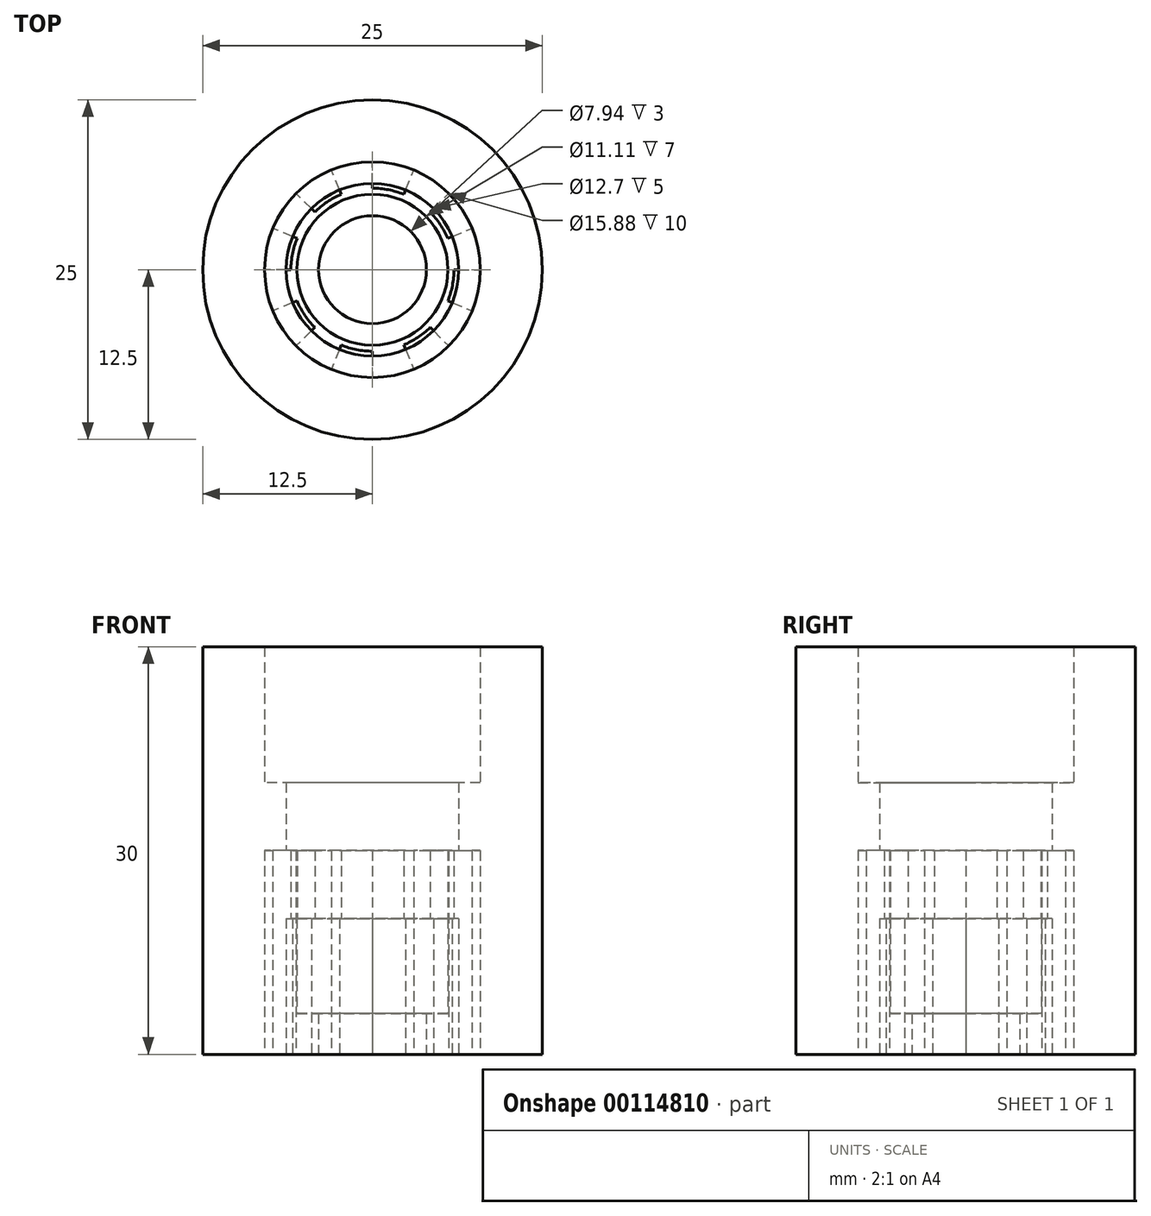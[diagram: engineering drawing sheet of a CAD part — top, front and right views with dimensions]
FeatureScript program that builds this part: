
annotation { "Feature Type Name" : "Feature", "Feature Type Description" : "" }
export const myFeature = defineFeature(function(context is Context, id is Id, definition is map)
    precondition{}
    {
        {
            var Q0;
            Q0=qCreatedBy(makeId("Top.planeOp"),FACE);
            var sketch = newSketch(context, id + "F0", { "sketchPlane" : qUnion([Q0])});
            skCircle(sketch, "E0", {"center": v(0, 0) * mm, "radius": 12.5 * mm});
            skCircle(sketch, "E1", {"center": v(0, 0) * mm, "radius": 7.94 * mm});
            skCircle(sketch, "E2", {"center": v(0, 0) * mm, "radius": 5.56 * mm});
            skCircle(sketch, "E3", {"center": v(0, 0) * mm, "radius": 3.97 * mm});
            skCircle(sketch, "E4", {"center": v(0, 0) * mm, "radius": 6.35 * mm});
            skCircle(sketch, "E5", {"center": v(0, 0) * mm, "radius": 6 * mm});
            skCircle(sketch, "E6", {"center": v(0, 0) * mm, "radius": 8.5 * mm});
            skLineSegment(sketch, "E7", {"start": v(0, 5.56) * mm, "end": v(0, 8.5) * mm});
            skLineSegment(sketch, "E8.1.0", {"start": v(-2.13, 5.13) * mm, "end": v(-3.25, 7.85) * mm});
            skLineSegment(sketch, "E8.2.0", {"start": v(-3.93, 3.93) * mm, "end": v(-6.01, 6.01) * mm});
            skLineSegment(sketch, "E9.1.3.0", {"start": v(-5.13, 2.13) * mm, "end": v(-7.85, 3.25) * mm});
            skLineSegment(sketch, "E9.1.4.0", {"start": v(-5.56, 0) * mm, "end": v(-8.5, 0) * mm});
            skLineSegment(sketch, "E9.1.5.0", {"start": v(-5.13, -2.13) * mm, "end": v(-7.85, -3.25) * mm});
            skLineSegment(sketch, "E9.1.6.0", {"start": v(-3.93, -3.93) * mm, "end": v(-6.01, -6.01) * mm});
            skLineSegment(sketch, "E9.1.7.0", {"start": v(-2.13, -5.13) * mm, "end": v(-3.25, -7.85) * mm});
            skLineSegment(sketch, "E9.1.8.0", {"start": v(0, -5.56) * mm, "end": v(0, -8.5) * mm});
            skLineSegment(sketch, "E9.1.9.0", {"start": v(2.13, -5.13) * mm, "end": v(3.25, -7.85) * mm});
            skLineSegment(sketch, "E9.1.10.0", {"start": v(3.93, -3.93) * mm, "end": v(6.01, -6.01) * mm});
            skLineSegment(sketch, "E9.1.11.0", {"start": v(5.13, -2.13) * mm, "end": v(7.85, -3.25) * mm});
            skLineSegment(sketch, "E10.1.12.0", {"start": v(5.56, 0) * mm, "end": v(8.5, 0) * mm});
            skLineSegment(sketch, "E10.1.13.0", {"start": v(5.13, 2.13) * mm, "end": v(7.85, 3.25) * mm});
            skLineSegment(sketch, "E10.1.14.0", {"start": v(3.93, 3.93) * mm, "end": v(6.01, 6.01) * mm});
            skLineSegment(sketch, "E10.1.15.0", {"start": v(2.13, 5.13) * mm, "end": v(3.25, 7.85) * mm});
            skSolve(sketch);
        }
        {
            var Q0;
            Q0=makeQuery(id+"F0.imprint","IMPRINT",FACE,{"disambiguationData":[TD([[makeQuery(id+"F0.imprint","IMPRINT",EDGE,{"derivedFrom":sQuery(id+"F0.wireOp",EDGE,"E3")}),-1.0]])]});
            extrude(context, id + "F1", {"entities" : qUnion([Q0]), "depth" : 3 * mm});
        }
        {
            var Q0;
            {var subQ0=sQuery(id+"F0.wireOp",EDGE,"E10.1.13.0");var subQ1=sQuery(id+"F0.wireOp",EDGE,"E2");var subQ2=makeQuery(id+"F0.imprint","INTERSECT",VERTEX,{"derivedFrom":[subQ1,subQ0]});Q0=makeQuery(id+"F0.imprint","IMPRINT",FACE,{"disambiguationData":[TD([[makeQuery(id+"F0.imprint","IMPRINT",EDGE,{"disambiguationData":[TD([[subQ2,-1.0]])],"derivedFrom":subQ1}),-1.0]])]});}
            var Q1;
            {var subQ0=sQuery(id+"F0.wireOp",EDGE,"E10.1.12.0");var subQ1=sQuery(id+"F0.wireOp",EDGE,"E2");var subQ2=makeQuery(id+"F0.imprint","INTERSECT",VERTEX,{"derivedFrom":[subQ1,subQ0]});Q1=makeQuery(id+"F0.imprint","IMPRINT",FACE,{"disambiguationData":[TD([[makeQuery(id+"F0.imprint","IMPRINT",EDGE,{"disambiguationData":[TD([[subQ2,-1.0]])],"derivedFrom":subQ1}),-1.0]])]});}
            var Q2;
            {var subQ0=sQuery(id+"F0.wireOp",EDGE,"E9.1.11.0");var subQ1=sQuery(id+"F0.wireOp",EDGE,"E2");var subQ2=makeQuery(id+"F0.imprint","INTERSECT",VERTEX,{"derivedFrom":[subQ1,subQ0]});Q2=makeQuery(id+"F0.imprint","IMPRINT",FACE,{"disambiguationData":[TD([[makeQuery(id+"F0.imprint","IMPRINT",EDGE,{"disambiguationData":[TD([[subQ2,-1.0]])],"derivedFrom":subQ1}),-1.0]])]});}
            var Q3;
            {var subQ0=sQuery(id+"F0.wireOp",EDGE,"E9.1.10.0");var subQ1=sQuery(id+"F0.wireOp",EDGE,"E2");var subQ2=makeQuery(id+"F0.imprint","INTERSECT",VERTEX,{"derivedFrom":[subQ1,subQ0]});Q3=makeQuery(id+"F0.imprint","IMPRINT",FACE,{"disambiguationData":[TD([[makeQuery(id+"F0.imprint","IMPRINT",EDGE,{"disambiguationData":[TD([[subQ2,-1.0]])],"derivedFrom":subQ1}),-1.0]])]});}
            var Q4;
            {var subQ0=sQuery(id+"F0.wireOp",EDGE,"E9.1.9.0");var subQ1=sQuery(id+"F0.wireOp",EDGE,"E2");var subQ2=makeQuery(id+"F0.imprint","INTERSECT",VERTEX,{"derivedFrom":[subQ1,subQ0]});Q4=makeQuery(id+"F0.imprint","IMPRINT",FACE,{"disambiguationData":[TD([[makeQuery(id+"F0.imprint","IMPRINT",EDGE,{"disambiguationData":[TD([[subQ2,-1.0]])],"derivedFrom":subQ1}),-1.0]])]});}
            var Q5;
            {var subQ0=sQuery(id+"F0.wireOp",EDGE,"E9.1.8.0");var subQ1=sQuery(id+"F0.wireOp",EDGE,"E2");var subQ2=makeQuery(id+"F0.imprint","INTERSECT",VERTEX,{"derivedFrom":[subQ1,subQ0]});Q5=makeQuery(id+"F0.imprint","IMPRINT",FACE,{"disambiguationData":[TD([[makeQuery(id+"F0.imprint","IMPRINT",EDGE,{"disambiguationData":[TD([[subQ2,-1.0]])],"derivedFrom":subQ1}),-1.0]])]});}
            var Q6;
            {var subQ0=sQuery(id+"F0.wireOp",EDGE,"E9.1.7.0");var subQ1=sQuery(id+"F0.wireOp",EDGE,"E2");var subQ2=makeQuery(id+"F0.imprint","INTERSECT",VERTEX,{"derivedFrom":[subQ1,subQ0]});Q6=makeQuery(id+"F0.imprint","IMPRINT",FACE,{"disambiguationData":[TD([[makeQuery(id+"F0.imprint","IMPRINT",EDGE,{"disambiguationData":[TD([[subQ2,-1.0]])],"derivedFrom":subQ1}),-1.0]])]});}
            var Q7;
            {var subQ0=sQuery(id+"F0.wireOp",EDGE,"E9.1.6.0");var subQ1=sQuery(id+"F0.wireOp",EDGE,"E2");var subQ2=makeQuery(id+"F0.imprint","INTERSECT",VERTEX,{"derivedFrom":[subQ1,subQ0]});Q7=makeQuery(id+"F0.imprint","IMPRINT",FACE,{"disambiguationData":[TD([[makeQuery(id+"F0.imprint","IMPRINT",EDGE,{"disambiguationData":[TD([[subQ2,-1.0]])],"derivedFrom":subQ1}),-1.0]])]});}
            var Q8;
            {var subQ0=sQuery(id+"F0.wireOp",EDGE,"E9.1.5.0");var subQ1=sQuery(id+"F0.wireOp",EDGE,"E2");var subQ2=makeQuery(id+"F0.imprint","INTERSECT",VERTEX,{"derivedFrom":[subQ1,subQ0]});Q8=makeQuery(id+"F0.imprint","IMPRINT",FACE,{"disambiguationData":[TD([[makeQuery(id+"F0.imprint","IMPRINT",EDGE,{"disambiguationData":[TD([[subQ2,-1.0]])],"derivedFrom":subQ1}),-1.0]])]});}
            var Q9;
            {var subQ0=sQuery(id+"F0.wireOp",EDGE,"E9.1.4.0");var subQ1=sQuery(id+"F0.wireOp",EDGE,"E2");var subQ2=makeQuery(id+"F0.imprint","INTERSECT",VERTEX,{"derivedFrom":[subQ1,subQ0]});Q9=makeQuery(id+"F0.imprint","IMPRINT",FACE,{"disambiguationData":[TD([[makeQuery(id+"F0.imprint","IMPRINT",EDGE,{"disambiguationData":[TD([[subQ2,-1.0]])],"derivedFrom":subQ1}),-1.0]])]});}
            var Q10;
            {var subQ0=sQuery(id+"F0.wireOp",EDGE,"E10.1.14.0");var subQ1=sQuery(id+"F0.wireOp",EDGE,"E2");var subQ2=makeQuery(id+"F0.imprint","INTERSECT",VERTEX,{"derivedFrom":[subQ1,subQ0]});Q10=makeQuery(id+"F0.imprint","IMPRINT",FACE,{"disambiguationData":[TD([[makeQuery(id+"F0.imprint","IMPRINT",EDGE,{"disambiguationData":[TD([[subQ2,-1.0]])],"derivedFrom":subQ1}),-1.0]])]});}
            var Q11;
            {var subQ0=sQuery(id+"F0.wireOp",EDGE,"E7");var subQ1=sQuery(id+"F0.wireOp",EDGE,"E2");var subQ2=makeQuery(id+"F0.imprint","INTERSECT",VERTEX,{"derivedFrom":[subQ1,subQ0]});Q11=makeQuery(id+"F0.imprint","IMPRINT",FACE,{"disambiguationData":[TD([[makeQuery(id+"F0.imprint","IMPRINT",EDGE,{"disambiguationData":[TD([[subQ2,1.0]])],"derivedFrom":subQ1}),-1.0]])]});}
            var Q12;
            {var subQ0=sQuery(id+"F0.wireOp",EDGE,"E7");var subQ1=sQuery(id+"F0.wireOp",EDGE,"E2");var subQ2=makeQuery(id+"F0.imprint","INTERSECT",VERTEX,{"derivedFrom":[subQ1,subQ0]});Q12=makeQuery(id+"F0.imprint","IMPRINT",FACE,{"disambiguationData":[TD([[makeQuery(id+"F0.imprint","IMPRINT",EDGE,{"disambiguationData":[TD([[subQ2,-1.0]])],"derivedFrom":subQ1}),-1.0]])]});}
            var Q13;
            {var subQ0=sQuery(id+"F0.wireOp",EDGE,"E8.1.0");var subQ1=sQuery(id+"F0.wireOp",EDGE,"E2");var subQ2=makeQuery(id+"F0.imprint","INTERSECT",VERTEX,{"derivedFrom":[subQ1,subQ0]});Q13=makeQuery(id+"F0.imprint","IMPRINT",FACE,{"disambiguationData":[TD([[makeQuery(id+"F0.imprint","IMPRINT",EDGE,{"disambiguationData":[TD([[subQ2,-1.0]])],"derivedFrom":subQ1}),-1.0]])]});}
            var Q14;
            {var subQ0=sQuery(id+"F0.wireOp",EDGE,"E8.2.0");var subQ1=sQuery(id+"F0.wireOp",EDGE,"E2");var subQ2=makeQuery(id+"F0.imprint","INTERSECT",VERTEX,{"derivedFrom":[subQ1,subQ0]});Q14=makeQuery(id+"F0.imprint","IMPRINT",FACE,{"disambiguationData":[TD([[makeQuery(id+"F0.imprint","IMPRINT",EDGE,{"disambiguationData":[TD([[subQ2,-1.0]])],"derivedFrom":subQ1}),-1.0]])]});}
            var Q15;
            {var subQ0=sQuery(id+"F0.wireOp",EDGE,"E9.1.3.0");var subQ1=sQuery(id+"F0.wireOp",EDGE,"E2");var subQ2=makeQuery(id+"F0.imprint","INTERSECT",VERTEX,{"derivedFrom":[subQ1,subQ0]});Q15=makeQuery(id+"F0.imprint","IMPRINT",FACE,{"disambiguationData":[TD([[makeQuery(id+"F0.imprint","IMPRINT",EDGE,{"disambiguationData":[TD([[subQ2,-1.0]])],"derivedFrom":subQ1}),-1.0]])]});}
            var Q16;
            {var subQ0=sQuery(id+"F0.wireOp",EDGE,"E7");var subQ1=sQuery(id+"F0.wireOp",EDGE,"E4");var subQ2=makeQuery(id+"F0.imprint","INTERSECT",VERTEX,{"derivedFrom":[subQ1,subQ0]});Q16=makeQuery(id+"F0.imprint","IMPRINT",FACE,{"disambiguationData":[TD([[makeQuery(id+"F0.imprint","IMPRINT",EDGE,{"disambiguationData":[TD([[subQ2,-1.0]])],"derivedFrom":subQ1}),1.0]])]});}
            var Q17;
            {var subQ0=sQuery(id+"F0.wireOp",EDGE,"E8.1.0");var subQ1=sQuery(id+"F0.wireOp",EDGE,"E4");var subQ2=makeQuery(id+"F0.imprint","INTERSECT",VERTEX,{"derivedFrom":[subQ1,subQ0]});Q17=makeQuery(id+"F0.imprint","IMPRINT",FACE,{"disambiguationData":[TD([[makeQuery(id+"F0.imprint","IMPRINT",EDGE,{"disambiguationData":[TD([[subQ2,-1.0]])],"derivedFrom":subQ1}),1.0]])]});}
            var Q18;
            {var subQ0=sQuery(id+"F0.wireOp",EDGE,"E8.2.0");var subQ1=sQuery(id+"F0.wireOp",EDGE,"E4");var subQ2=makeQuery(id+"F0.imprint","INTERSECT",VERTEX,{"derivedFrom":[subQ1,subQ0]});Q18=makeQuery(id+"F0.imprint","IMPRINT",FACE,{"disambiguationData":[TD([[makeQuery(id+"F0.imprint","IMPRINT",EDGE,{"disambiguationData":[TD([[subQ2,-1.0]])],"derivedFrom":subQ1}),1.0]])]});}
            var Q19;
            {var subQ0=sQuery(id+"F0.wireOp",EDGE,"E10.1.15.0");var subQ1=sQuery(id+"F0.wireOp",EDGE,"E4");var subQ2=makeQuery(id+"F0.imprint","INTERSECT",VERTEX,{"derivedFrom":[subQ1,subQ0]});Q19=makeQuery(id+"F0.imprint","IMPRINT",FACE,{"disambiguationData":[TD([[makeQuery(id+"F0.imprint","IMPRINT",EDGE,{"disambiguationData":[TD([[subQ2,-1.0]])],"derivedFrom":subQ1}),1.0]])]});}
            var Q20;
            {var subQ0=sQuery(id+"F0.wireOp",EDGE,"E10.1.14.0");var subQ1=sQuery(id+"F0.wireOp",EDGE,"E4");var subQ2=makeQuery(id+"F0.imprint","INTERSECT",VERTEX,{"derivedFrom":[subQ1,subQ0]});Q20=makeQuery(id+"F0.imprint","IMPRINT",FACE,{"disambiguationData":[TD([[makeQuery(id+"F0.imprint","IMPRINT",EDGE,{"disambiguationData":[TD([[subQ2,-1.0]])],"derivedFrom":subQ1}),1.0]])]});}
            var Q21;
            {var subQ0=sQuery(id+"F0.wireOp",EDGE,"E10.1.13.0");var subQ1=sQuery(id+"F0.wireOp",EDGE,"E4");var subQ2=makeQuery(id+"F0.imprint","INTERSECT",VERTEX,{"derivedFrom":[subQ1,subQ0]});Q21=makeQuery(id+"F0.imprint","IMPRINT",FACE,{"disambiguationData":[TD([[makeQuery(id+"F0.imprint","IMPRINT",EDGE,{"disambiguationData":[TD([[subQ2,-1.0]])],"derivedFrom":subQ1}),1.0]])]});}
            var Q22;
            {var subQ0=sQuery(id+"F0.wireOp",EDGE,"E10.1.13.0");var subQ1=sQuery(id+"F0.wireOp",EDGE,"E4");var subQ2=makeQuery(id+"F0.imprint","INTERSECT",VERTEX,{"derivedFrom":[subQ1,subQ0]});Q22=makeQuery(id+"F0.imprint","IMPRINT",FACE,{"disambiguationData":[TD([[makeQuery(id+"F0.imprint","IMPRINT",EDGE,{"disambiguationData":[TD([[subQ2,1.0]])],"derivedFrom":subQ1}),1.0]])]});}
            var Q23;
            {var subQ0=sQuery(id+"F0.wireOp",EDGE,"E10.1.12.0");var subQ1=sQuery(id+"F0.wireOp",EDGE,"E4");var subQ2=makeQuery(id+"F0.imprint","INTERSECT",VERTEX,{"derivedFrom":[subQ1,subQ0]});Q23=makeQuery(id+"F0.imprint","IMPRINT",FACE,{"disambiguationData":[TD([[makeQuery(id+"F0.imprint","IMPRINT",EDGE,{"disambiguationData":[TD([[subQ2,1.0]])],"derivedFrom":subQ1}),1.0]])]});}
            var Q24;
            {var subQ0=sQuery(id+"F0.wireOp",EDGE,"E9.1.10.0");var subQ1=sQuery(id+"F0.wireOp",EDGE,"E4");var subQ2=makeQuery(id+"F0.imprint","INTERSECT",VERTEX,{"derivedFrom":[subQ1,subQ0]});Q24=makeQuery(id+"F0.imprint","IMPRINT",FACE,{"disambiguationData":[TD([[makeQuery(id+"F0.imprint","IMPRINT",EDGE,{"disambiguationData":[TD([[subQ2,-1.0]])],"derivedFrom":subQ1}),1.0]])]});}
            var Q25;
            {var subQ0=sQuery(id+"F0.wireOp",EDGE,"E9.1.9.0");var subQ1=sQuery(id+"F0.wireOp",EDGE,"E4");var subQ2=makeQuery(id+"F0.imprint","INTERSECT",VERTEX,{"derivedFrom":[subQ1,subQ0]});Q25=makeQuery(id+"F0.imprint","IMPRINT",FACE,{"disambiguationData":[TD([[makeQuery(id+"F0.imprint","IMPRINT",EDGE,{"disambiguationData":[TD([[subQ2,-1.0]])],"derivedFrom":subQ1}),1.0]])]});}
            var Q26;
            {var subQ0=sQuery(id+"F0.wireOp",EDGE,"E9.1.8.0");var subQ1=sQuery(id+"F0.wireOp",EDGE,"E4");var subQ2=makeQuery(id+"F0.imprint","INTERSECT",VERTEX,{"derivedFrom":[subQ1,subQ0]});Q26=makeQuery(id+"F0.imprint","IMPRINT",FACE,{"disambiguationData":[TD([[makeQuery(id+"F0.imprint","IMPRINT",EDGE,{"disambiguationData":[TD([[subQ2,-1.0]])],"derivedFrom":subQ1}),1.0]])]});}
            var Q27;
            {var subQ0=sQuery(id+"F0.wireOp",EDGE,"E9.1.7.0");var subQ1=sQuery(id+"F0.wireOp",EDGE,"E4");var subQ2=makeQuery(id+"F0.imprint","INTERSECT",VERTEX,{"derivedFrom":[subQ1,subQ0]});Q27=makeQuery(id+"F0.imprint","IMPRINT",FACE,{"disambiguationData":[TD([[makeQuery(id+"F0.imprint","IMPRINT",EDGE,{"disambiguationData":[TD([[subQ2,-1.0]])],"derivedFrom":subQ1}),1.0]])]});}
            var Q28;
            {var subQ0=sQuery(id+"F0.wireOp",EDGE,"E9.1.6.0");var subQ1=sQuery(id+"F0.wireOp",EDGE,"E4");var subQ2=makeQuery(id+"F0.imprint","INTERSECT",VERTEX,{"derivedFrom":[subQ1,subQ0]});Q28=makeQuery(id+"F0.imprint","IMPRINT",FACE,{"disambiguationData":[TD([[makeQuery(id+"F0.imprint","IMPRINT",EDGE,{"disambiguationData":[TD([[subQ2,-1.0]])],"derivedFrom":subQ1}),1.0]])]});}
            var Q29;
            {var subQ0=sQuery(id+"F0.wireOp",EDGE,"E9.1.5.0");var subQ1=sQuery(id+"F0.wireOp",EDGE,"E4");var subQ2=makeQuery(id+"F0.imprint","INTERSECT",VERTEX,{"derivedFrom":[subQ1,subQ0]});Q29=makeQuery(id+"F0.imprint","IMPRINT",FACE,{"disambiguationData":[TD([[makeQuery(id+"F0.imprint","IMPRINT",EDGE,{"disambiguationData":[TD([[subQ2,-1.0]])],"derivedFrom":subQ1}),1.0]])]});}
            var Q30;
            {var subQ0=sQuery(id+"F0.wireOp",EDGE,"E9.1.4.0");var subQ1=sQuery(id+"F0.wireOp",EDGE,"E4");var subQ2=makeQuery(id+"F0.imprint","INTERSECT",VERTEX,{"derivedFrom":[subQ1,subQ0]});Q30=makeQuery(id+"F0.imprint","IMPRINT",FACE,{"disambiguationData":[TD([[makeQuery(id+"F0.imprint","IMPRINT",EDGE,{"disambiguationData":[TD([[subQ2,-1.0]])],"derivedFrom":subQ1}),1.0]])]});}
            var Q31;
            {var subQ0=sQuery(id+"F0.wireOp",EDGE,"E9.1.3.0");var subQ1=sQuery(id+"F0.wireOp",EDGE,"E4");var subQ2=makeQuery(id+"F0.imprint","INTERSECT",VERTEX,{"derivedFrom":[subQ1,subQ0]});Q31=makeQuery(id+"F0.imprint","IMPRINT",FACE,{"disambiguationData":[TD([[makeQuery(id+"F0.imprint","IMPRINT",EDGE,{"disambiguationData":[TD([[subQ2,-1.0]])],"derivedFrom":subQ1}),1.0]])]});}
            extrude(context, id + "F2", {"entities" : qUnion([Q0, Q1, Q2, Q3, Q4, Q5, Q6, Q7, Q8, Q9, Q10, Q11, Q12, Q13, Q14, Q15, Q16, Q17, Q18, Q19, Q20, Q21, Q22, Q23, Q24, Q25, Q26, Q27, Q28, Q29, Q30, Q31]), "operationType" : NewBodyOperationType.ADD, "depth" : 10 * mm});
        }
        {
            var Q0;
            {var subQ0=sQuery(id+"F0.wireOp",EDGE,"E10.1.15.0");var subQ1=sQuery(id+"F0.wireOp",EDGE,"E4");var subQ2=makeQuery(id+"F0.imprint","INTERSECT",VERTEX,{"derivedFrom":[subQ1,subQ0]});Q0=makeQuery(id+"F0.imprint","IMPRINT",FACE,{"disambiguationData":[TD([[makeQuery(id+"F0.imprint","IMPRINT",EDGE,{"disambiguationData":[TD([[subQ2,-1.0]])],"derivedFrom":subQ1}),1.0]])]});}
            var Q1;
            {var subQ0=sQuery(id+"F0.wireOp",EDGE,"E10.1.13.0");var subQ1=sQuery(id+"F0.wireOp",EDGE,"E4");var subQ2=makeQuery(id+"F0.imprint","INTERSECT",VERTEX,{"derivedFrom":[subQ1,subQ0]});Q1=makeQuery(id+"F0.imprint","IMPRINT",FACE,{"disambiguationData":[TD([[makeQuery(id+"F0.imprint","IMPRINT",EDGE,{"disambiguationData":[TD([[subQ2,-1.0]])],"derivedFrom":subQ1}),1.0]])]});}
            var Q2;
            {var subQ0=sQuery(id+"F0.wireOp",EDGE,"E10.1.12.0");var subQ1=sQuery(id+"F0.wireOp",EDGE,"E4");var subQ2=makeQuery(id+"F0.imprint","INTERSECT",VERTEX,{"derivedFrom":[subQ1,subQ0]});Q2=makeQuery(id+"F0.imprint","IMPRINT",FACE,{"disambiguationData":[TD([[makeQuery(id+"F0.imprint","IMPRINT",EDGE,{"disambiguationData":[TD([[subQ2,1.0]])],"derivedFrom":subQ1}),1.0]])]});}
            var Q3;
            {var subQ0=sQuery(id+"F0.wireOp",EDGE,"E9.1.9.0");var subQ1=sQuery(id+"F0.wireOp",EDGE,"E4");var subQ2=makeQuery(id+"F0.imprint","INTERSECT",VERTEX,{"derivedFrom":[subQ1,subQ0]});Q3=makeQuery(id+"F0.imprint","IMPRINT",FACE,{"disambiguationData":[TD([[makeQuery(id+"F0.imprint","IMPRINT",EDGE,{"disambiguationData":[TD([[subQ2,-1.0]])],"derivedFrom":subQ1}),1.0]])]});}
            var Q4;
            {var subQ0=sQuery(id+"F0.wireOp",EDGE,"E9.1.7.0");var subQ1=sQuery(id+"F0.wireOp",EDGE,"E4");var subQ2=makeQuery(id+"F0.imprint","INTERSECT",VERTEX,{"derivedFrom":[subQ1,subQ0]});Q4=makeQuery(id+"F0.imprint","IMPRINT",FACE,{"disambiguationData":[TD([[makeQuery(id+"F0.imprint","IMPRINT",EDGE,{"disambiguationData":[TD([[subQ2,-1.0]])],"derivedFrom":subQ1}),1.0]])]});}
            var Q5;
            {var subQ0=sQuery(id+"F0.wireOp",EDGE,"E9.1.5.0");var subQ1=sQuery(id+"F0.wireOp",EDGE,"E4");var subQ2=makeQuery(id+"F0.imprint","INTERSECT",VERTEX,{"derivedFrom":[subQ1,subQ0]});Q5=makeQuery(id+"F0.imprint","IMPRINT",FACE,{"disambiguationData":[TD([[makeQuery(id+"F0.imprint","IMPRINT",EDGE,{"disambiguationData":[TD([[subQ2,-1.0]])],"derivedFrom":subQ1}),1.0]])]});}
            var Q6;
            {var subQ0=sQuery(id+"F0.wireOp",EDGE,"E9.1.3.0");var subQ1=sQuery(id+"F0.wireOp",EDGE,"E4");var subQ2=makeQuery(id+"F0.imprint","INTERSECT",VERTEX,{"derivedFrom":[subQ1,subQ0]});Q6=makeQuery(id+"F0.imprint","IMPRINT",FACE,{"disambiguationData":[TD([[makeQuery(id+"F0.imprint","IMPRINT",EDGE,{"disambiguationData":[TD([[subQ2,-1.0]])],"derivedFrom":subQ1}),1.0]])]});}
            var Q7;
            {var subQ0=sQuery(id+"F0.wireOp",EDGE,"E8.1.0");var subQ1=sQuery(id+"F0.wireOp",EDGE,"E4");var subQ2=makeQuery(id+"F0.imprint","INTERSECT",VERTEX,{"derivedFrom":[subQ1,subQ0]});Q7=makeQuery(id+"F0.imprint","IMPRINT",FACE,{"disambiguationData":[TD([[makeQuery(id+"F0.imprint","IMPRINT",EDGE,{"disambiguationData":[TD([[subQ2,-1.0]])],"derivedFrom":subQ1}),1.0]])]});}
            extrude(context, id + "F3", {"entities" : qUnion([Q0, Q1, Q2, Q3, Q4, Q5, Q6, Q7]), "operationType" : NewBodyOperationType.ADD, "depth" : 15 * mm});
        }
        {
            var Q0;
            {var subQ0=sQuery(id+"F0.wireOp",EDGE,"E10.1.15.0");var subQ1=sQuery(id+"F0.wireOp",EDGE,"E1");var subQ2=makeQuery(id+"F0.imprint","INTERSECT",VERTEX,{"derivedFrom":[subQ1,subQ0]});Q0=makeQuery(id+"F0.imprint","IMPRINT",FACE,{"disambiguationData":[TD([[makeQuery(id+"F0.imprint","IMPRINT",EDGE,{"disambiguationData":[TD([[subQ2,-1.0]])],"derivedFrom":subQ1}),1.0]])]});}
            var Q1;
            {var subQ0=sQuery(id+"F0.wireOp",EDGE,"E10.1.13.0");var subQ1=sQuery(id+"F0.wireOp",EDGE,"E1");var subQ2=makeQuery(id+"F0.imprint","INTERSECT",VERTEX,{"derivedFrom":[subQ1,subQ0]});Q1=makeQuery(id+"F0.imprint","IMPRINT",FACE,{"disambiguationData":[TD([[makeQuery(id+"F0.imprint","IMPRINT",EDGE,{"disambiguationData":[TD([[subQ2,-1.0]])],"derivedFrom":subQ1}),1.0]])]});}
            var Q2;
            {var subQ0=sQuery(id+"F0.wireOp",EDGE,"E10.1.12.0");var subQ1=sQuery(id+"F0.wireOp",EDGE,"E1");var subQ2=makeQuery(id+"F0.imprint","INTERSECT",VERTEX,{"derivedFrom":[subQ1,subQ0]});Q2=makeQuery(id+"F0.imprint","IMPRINT",FACE,{"disambiguationData":[TD([[makeQuery(id+"F0.imprint","IMPRINT",EDGE,{"disambiguationData":[TD([[subQ2,1.0]])],"derivedFrom":subQ1}),1.0]])]});}
            var Q3;
            {var subQ0=sQuery(id+"F0.wireOp",EDGE,"E9.1.9.0");var subQ1=sQuery(id+"F0.wireOp",EDGE,"E1");var subQ2=makeQuery(id+"F0.imprint","INTERSECT",VERTEX,{"derivedFrom":[subQ1,subQ0]});Q3=makeQuery(id+"F0.imprint","IMPRINT",FACE,{"disambiguationData":[TD([[makeQuery(id+"F0.imprint","IMPRINT",EDGE,{"disambiguationData":[TD([[subQ2,-1.0]])],"derivedFrom":subQ1}),1.0]])]});}
            var Q4;
            {var subQ0=sQuery(id+"F0.wireOp",EDGE,"E9.1.7.0");var subQ1=sQuery(id+"F0.wireOp",EDGE,"E1");var subQ2=makeQuery(id+"F0.imprint","INTERSECT",VERTEX,{"derivedFrom":[subQ1,subQ0]});Q4=makeQuery(id+"F0.imprint","IMPRINT",FACE,{"disambiguationData":[TD([[makeQuery(id+"F0.imprint","IMPRINT",EDGE,{"disambiguationData":[TD([[subQ2,-1.0]])],"derivedFrom":subQ1}),1.0]])]});}
            var Q5;
            {var subQ0=sQuery(id+"F0.wireOp",EDGE,"E9.1.5.0");var subQ1=sQuery(id+"F0.wireOp",EDGE,"E1");var subQ2=makeQuery(id+"F0.imprint","INTERSECT",VERTEX,{"derivedFrom":[subQ1,subQ0]});Q5=makeQuery(id+"F0.imprint","IMPRINT",FACE,{"disambiguationData":[TD([[makeQuery(id+"F0.imprint","IMPRINT",EDGE,{"disambiguationData":[TD([[subQ2,-1.0]])],"derivedFrom":subQ1}),1.0]])]});}
            var Q6;
            {var subQ0=sQuery(id+"F0.wireOp",EDGE,"E9.1.3.0");var subQ1=sQuery(id+"F0.wireOp",EDGE,"E1");var subQ2=makeQuery(id+"F0.imprint","INTERSECT",VERTEX,{"derivedFrom":[subQ1,subQ0]});Q6=makeQuery(id+"F0.imprint","IMPRINT",FACE,{"disambiguationData":[TD([[makeQuery(id+"F0.imprint","IMPRINT",EDGE,{"disambiguationData":[TD([[subQ2,-1.0]])],"derivedFrom":subQ1}),1.0]])]});}
            var Q7;
            {var subQ0=sQuery(id+"F0.wireOp",EDGE,"E8.1.0");var subQ1=sQuery(id+"F0.wireOp",EDGE,"E1");var subQ2=makeQuery(id+"F0.imprint","INTERSECT",VERTEX,{"derivedFrom":[subQ1,subQ0]});Q7=makeQuery(id+"F0.imprint","IMPRINT",FACE,{"disambiguationData":[TD([[makeQuery(id+"F0.imprint","IMPRINT",EDGE,{"disambiguationData":[TD([[subQ2,-1.0]])],"derivedFrom":subQ1}),1.0]])]});}
            extrude(context, id + "F4", {"entities" : qUnion([Q0, Q1, Q2, Q3, Q4, Q5, Q6, Q7]), "operationType" : NewBodyOperationType.ADD, "depth" : 20 * mm});
        }
        {
            var Q0;
            {var subQ0=sQuery(id+"F0.wireOp",EDGE,"E10.1.14.0");var subQ1=sQuery(id+"F0.wireOp",EDGE,"E1");var subQ2=makeQuery(id+"F0.imprint","INTERSECT",VERTEX,{"derivedFrom":[subQ1,subQ0]});Q0=makeQuery(id+"F0.imprint","IMPRINT",FACE,{"disambiguationData":[TD([[makeQuery(id+"F0.imprint","IMPRINT",EDGE,{"disambiguationData":[TD([[subQ2,-1.0]])],"derivedFrom":subQ1}),1.0]])]});}
            var Q1;
            {var subQ0=sQuery(id+"F0.wireOp",EDGE,"E10.1.13.0");var subQ1=sQuery(id+"F0.wireOp",EDGE,"E1");var subQ2=makeQuery(id+"F0.imprint","INTERSECT",VERTEX,{"derivedFrom":[subQ1,subQ0]});Q1=makeQuery(id+"F0.imprint","IMPRINT",FACE,{"disambiguationData":[TD([[makeQuery(id+"F0.imprint","IMPRINT",EDGE,{"disambiguationData":[TD([[subQ2,1.0]])],"derivedFrom":subQ1}),1.0]])]});}
            var Q2;
            {var subQ0=sQuery(id+"F0.wireOp",EDGE,"E9.1.10.0");var subQ1=sQuery(id+"F0.wireOp",EDGE,"E1");var subQ2=makeQuery(id+"F0.imprint","INTERSECT",VERTEX,{"derivedFrom":[subQ1,subQ0]});Q2=makeQuery(id+"F0.imprint","IMPRINT",FACE,{"disambiguationData":[TD([[makeQuery(id+"F0.imprint","IMPRINT",EDGE,{"disambiguationData":[TD([[subQ2,-1.0]])],"derivedFrom":subQ1}),1.0]])]});}
            var Q3;
            {var subQ0=sQuery(id+"F0.wireOp",EDGE,"E9.1.8.0");var subQ1=sQuery(id+"F0.wireOp",EDGE,"E1");var subQ2=makeQuery(id+"F0.imprint","INTERSECT",VERTEX,{"derivedFrom":[subQ1,subQ0]});Q3=makeQuery(id+"F0.imprint","IMPRINT",FACE,{"disambiguationData":[TD([[makeQuery(id+"F0.imprint","IMPRINT",EDGE,{"disambiguationData":[TD([[subQ2,-1.0]])],"derivedFrom":subQ1}),1.0]])]});}
            var Q4;
            {var subQ0=sQuery(id+"F0.wireOp",EDGE,"E9.1.6.0");var subQ1=sQuery(id+"F0.wireOp",EDGE,"E1");var subQ2=makeQuery(id+"F0.imprint","INTERSECT",VERTEX,{"derivedFrom":[subQ1,subQ0]});Q4=makeQuery(id+"F0.imprint","IMPRINT",FACE,{"disambiguationData":[TD([[makeQuery(id+"F0.imprint","IMPRINT",EDGE,{"disambiguationData":[TD([[subQ2,-1.0]])],"derivedFrom":subQ1}),1.0]])]});}
            var Q5;
            {var subQ0=sQuery(id+"F0.wireOp",EDGE,"E9.1.4.0");var subQ1=sQuery(id+"F0.wireOp",EDGE,"E1");var subQ2=makeQuery(id+"F0.imprint","INTERSECT",VERTEX,{"derivedFrom":[subQ1,subQ0]});Q5=makeQuery(id+"F0.imprint","IMPRINT",FACE,{"disambiguationData":[TD([[makeQuery(id+"F0.imprint","IMPRINT",EDGE,{"disambiguationData":[TD([[subQ2,-1.0]])],"derivedFrom":subQ1}),1.0]])]});}
            var Q6;
            {var subQ0=sQuery(id+"F0.wireOp",EDGE,"E8.2.0");var subQ1=sQuery(id+"F0.wireOp",EDGE,"E1");var subQ2=makeQuery(id+"F0.imprint","INTERSECT",VERTEX,{"derivedFrom":[subQ1,subQ0]});Q6=makeQuery(id+"F0.imprint","IMPRINT",FACE,{"disambiguationData":[TD([[makeQuery(id+"F0.imprint","IMPRINT",EDGE,{"disambiguationData":[TD([[subQ2,-1.0]])],"derivedFrom":subQ1}),1.0]])]});}
            var Q7;
            {var subQ0=sQuery(id+"F0.wireOp",EDGE,"E7");var subQ1=sQuery(id+"F0.wireOp",EDGE,"E1");var subQ2=makeQuery(id+"F0.imprint","INTERSECT",VERTEX,{"derivedFrom":[subQ1,subQ0]});Q7=makeQuery(id+"F0.imprint","IMPRINT",FACE,{"disambiguationData":[TD([[makeQuery(id+"F0.imprint","IMPRINT",EDGE,{"disambiguationData":[TD([[subQ2,-1.0]])],"derivedFrom":subQ1}),1.0]])]});}
            extrude(context, id + "F5", {"entities" : qUnion([Q0, Q1, Q2, Q3, Q4, Q5, Q6, Q7]), "operationType" : NewBodyOperationType.ADD, "depth" : 20 * mm, "hasSecondDirection" : true, "secondDirectionOppositeDirection" : false, "secondDirectionDepth" : 15 * mm});
        }
        {
            var Q0;
            {var subQ0=sQuery(id+"F0.wireOp",EDGE,"E10.1.15.0");var subQ1=sQuery(id+"F0.wireOp",EDGE,"E1");var subQ2=makeQuery(id+"F0.imprint","INTERSECT",VERTEX,{"derivedFrom":[subQ1,subQ0]});Q0=makeQuery(id+"F0.imprint","IMPRINT",FACE,{"disambiguationData":[TD([[makeQuery(id+"F0.imprint","IMPRINT",EDGE,{"disambiguationData":[TD([[subQ2,-1.0]])],"derivedFrom":subQ1}),-1.0]])]});}
            var Q1;
            {var subQ0=sQuery(id+"F0.wireOp",EDGE,"E10.1.14.0");var subQ1=sQuery(id+"F0.wireOp",EDGE,"E1");var subQ2=makeQuery(id+"F0.imprint","INTERSECT",VERTEX,{"derivedFrom":[subQ1,subQ0]});Q1=makeQuery(id+"F0.imprint","IMPRINT",FACE,{"disambiguationData":[TD([[makeQuery(id+"F0.imprint","IMPRINT",EDGE,{"disambiguationData":[TD([[subQ2,-1.0]])],"derivedFrom":subQ1}),-1.0]])]});}
            var Q2;
            {var subQ0=sQuery(id+"F0.wireOp",EDGE,"E10.1.13.0");var subQ1=sQuery(id+"F0.wireOp",EDGE,"E1");var subQ2=makeQuery(id+"F0.imprint","INTERSECT",VERTEX,{"derivedFrom":[subQ1,subQ0]});Q2=makeQuery(id+"F0.imprint","IMPRINT",FACE,{"disambiguationData":[TD([[makeQuery(id+"F0.imprint","IMPRINT",EDGE,{"disambiguationData":[TD([[subQ2,-1.0]])],"derivedFrom":subQ1}),-1.0]])]});}
            var Q3;
            {var subQ0=sQuery(id+"F0.wireOp",EDGE,"E10.1.13.0");var subQ1=sQuery(id+"F0.wireOp",EDGE,"E1");var subQ2=makeQuery(id+"F0.imprint","INTERSECT",VERTEX,{"derivedFrom":[subQ1,subQ0]});Q3=makeQuery(id+"F0.imprint","IMPRINT",FACE,{"disambiguationData":[TD([[makeQuery(id+"F0.imprint","IMPRINT",EDGE,{"disambiguationData":[TD([[subQ2,1.0]])],"derivedFrom":subQ1}),-1.0]])]});}
            var Q4;
            {var subQ0=sQuery(id+"F0.wireOp",EDGE,"E10.1.12.0");var subQ1=sQuery(id+"F0.wireOp",EDGE,"E1");var subQ2=makeQuery(id+"F0.imprint","INTERSECT",VERTEX,{"derivedFrom":[subQ1,subQ0]});Q4=makeQuery(id+"F0.imprint","IMPRINT",FACE,{"disambiguationData":[TD([[makeQuery(id+"F0.imprint","IMPRINT",EDGE,{"disambiguationData":[TD([[subQ2,1.0]])],"derivedFrom":subQ1}),-1.0]])]});}
            var Q5;
            {var subQ0=sQuery(id+"F0.wireOp",EDGE,"E9.1.10.0");var subQ1=sQuery(id+"F0.wireOp",EDGE,"E1");var subQ2=makeQuery(id+"F0.imprint","INTERSECT",VERTEX,{"derivedFrom":[subQ1,subQ0]});Q5=makeQuery(id+"F0.imprint","IMPRINT",FACE,{"disambiguationData":[TD([[makeQuery(id+"F0.imprint","IMPRINT",EDGE,{"disambiguationData":[TD([[subQ2,-1.0]])],"derivedFrom":subQ1}),-1.0]])]});}
            var Q6;
            {var subQ0=sQuery(id+"F0.wireOp",EDGE,"E9.1.9.0");var subQ1=sQuery(id+"F0.wireOp",EDGE,"E1");var subQ2=makeQuery(id+"F0.imprint","INTERSECT",VERTEX,{"derivedFrom":[subQ1,subQ0]});Q6=makeQuery(id+"F0.imprint","IMPRINT",FACE,{"disambiguationData":[TD([[makeQuery(id+"F0.imprint","IMPRINT",EDGE,{"disambiguationData":[TD([[subQ2,-1.0]])],"derivedFrom":subQ1}),-1.0]])]});}
            var Q7;
            {var subQ0=sQuery(id+"F0.wireOp",EDGE,"E9.1.8.0");var subQ1=sQuery(id+"F0.wireOp",EDGE,"E1");var subQ2=makeQuery(id+"F0.imprint","INTERSECT",VERTEX,{"derivedFrom":[subQ1,subQ0]});Q7=makeQuery(id+"F0.imprint","IMPRINT",FACE,{"disambiguationData":[TD([[makeQuery(id+"F0.imprint","IMPRINT",EDGE,{"disambiguationData":[TD([[subQ2,-1.0]])],"derivedFrom":subQ1}),-1.0]])]});}
            var Q8;
            {var subQ0=sQuery(id+"F0.wireOp",EDGE,"E9.1.7.0");var subQ1=sQuery(id+"F0.wireOp",EDGE,"E1");var subQ2=makeQuery(id+"F0.imprint","INTERSECT",VERTEX,{"derivedFrom":[subQ1,subQ0]});Q8=makeQuery(id+"F0.imprint","IMPRINT",FACE,{"disambiguationData":[TD([[makeQuery(id+"F0.imprint","IMPRINT",EDGE,{"disambiguationData":[TD([[subQ2,-1.0]])],"derivedFrom":subQ1}),-1.0]])]});}
            var Q9;
            {var subQ0=sQuery(id+"F0.wireOp",EDGE,"E9.1.6.0");var subQ1=sQuery(id+"F0.wireOp",EDGE,"E1");var subQ2=makeQuery(id+"F0.imprint","INTERSECT",VERTEX,{"derivedFrom":[subQ1,subQ0]});Q9=makeQuery(id+"F0.imprint","IMPRINT",FACE,{"disambiguationData":[TD([[makeQuery(id+"F0.imprint","IMPRINT",EDGE,{"disambiguationData":[TD([[subQ2,-1.0]])],"derivedFrom":subQ1}),-1.0]])]});}
            var Q10;
            {var subQ0=sQuery(id+"F0.wireOp",EDGE,"E9.1.5.0");var subQ1=sQuery(id+"F0.wireOp",EDGE,"E1");var subQ2=makeQuery(id+"F0.imprint","INTERSECT",VERTEX,{"derivedFrom":[subQ1,subQ0]});Q10=makeQuery(id+"F0.imprint","IMPRINT",FACE,{"disambiguationData":[TD([[makeQuery(id+"F0.imprint","IMPRINT",EDGE,{"disambiguationData":[TD([[subQ2,-1.0]])],"derivedFrom":subQ1}),-1.0]])]});}
            var Q11;
            {var subQ0=sQuery(id+"F0.wireOp",EDGE,"E9.1.4.0");var subQ1=sQuery(id+"F0.wireOp",EDGE,"E1");var subQ2=makeQuery(id+"F0.imprint","INTERSECT",VERTEX,{"derivedFrom":[subQ1,subQ0]});Q11=makeQuery(id+"F0.imprint","IMPRINT",FACE,{"disambiguationData":[TD([[makeQuery(id+"F0.imprint","IMPRINT",EDGE,{"disambiguationData":[TD([[subQ2,-1.0]])],"derivedFrom":subQ1}),-1.0]])]});}
            var Q12;
            {var subQ0=sQuery(id+"F0.wireOp",EDGE,"E9.1.3.0");var subQ1=sQuery(id+"F0.wireOp",EDGE,"E1");var subQ2=makeQuery(id+"F0.imprint","INTERSECT",VERTEX,{"derivedFrom":[subQ1,subQ0]});Q12=makeQuery(id+"F0.imprint","IMPRINT",FACE,{"disambiguationData":[TD([[makeQuery(id+"F0.imprint","IMPRINT",EDGE,{"disambiguationData":[TD([[subQ2,-1.0]])],"derivedFrom":subQ1}),-1.0]])]});}
            var Q13;
            {var subQ0=sQuery(id+"F0.wireOp",EDGE,"E8.2.0");var subQ1=sQuery(id+"F0.wireOp",EDGE,"E1");var subQ2=makeQuery(id+"F0.imprint","INTERSECT",VERTEX,{"derivedFrom":[subQ1,subQ0]});Q13=makeQuery(id+"F0.imprint","IMPRINT",FACE,{"disambiguationData":[TD([[makeQuery(id+"F0.imprint","IMPRINT",EDGE,{"disambiguationData":[TD([[subQ2,-1.0]])],"derivedFrom":subQ1}),-1.0]])]});}
            var Q14;
            {var subQ0=sQuery(id+"F0.wireOp",EDGE,"E8.1.0");var subQ1=sQuery(id+"F0.wireOp",EDGE,"E1");var subQ2=makeQuery(id+"F0.imprint","INTERSECT",VERTEX,{"derivedFrom":[subQ1,subQ0]});Q14=makeQuery(id+"F0.imprint","IMPRINT",FACE,{"disambiguationData":[TD([[makeQuery(id+"F0.imprint","IMPRINT",EDGE,{"disambiguationData":[TD([[subQ2,-1.0]])],"derivedFrom":subQ1}),-1.0]])]});}
            var Q15;
            {var subQ0=sQuery(id+"F0.wireOp",EDGE,"E7");var subQ1=sQuery(id+"F0.wireOp",EDGE,"E1");var subQ2=makeQuery(id+"F0.imprint","INTERSECT",VERTEX,{"derivedFrom":[subQ1,subQ0]});Q15=makeQuery(id+"F0.imprint","IMPRINT",FACE,{"disambiguationData":[TD([[makeQuery(id+"F0.imprint","IMPRINT",EDGE,{"disambiguationData":[TD([[subQ2,-1.0]])],"derivedFrom":subQ1}),-1.0]])]});}
            extrude(context, id + "F6", {"entities" : qUnion([Q0, Q1, Q2, Q3, Q4, Q5, Q6, Q7, Q8, Q9, Q10, Q11, Q12, Q13, Q14, Q15]), "operationType" : NewBodyOperationType.ADD, "depth" : 30 * mm});
        }
        {
            var Q0;
            Q0=makeQuery(id+"F0.imprint","IMPRINT",FACE,{"disambiguationData":[TD([[makeQuery(id+"F0.imprint","IMPRINT",EDGE,{"derivedFrom":sQuery(id+"F0.wireOp",EDGE,"E0")}),1.0]])]});
            extrude(context, id + "F7", {"entities" : qUnion([Q0]), "operationType" : NewBodyOperationType.ADD, "depth" : 30 * mm});
        }
    });
